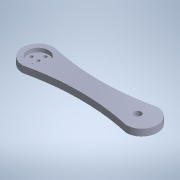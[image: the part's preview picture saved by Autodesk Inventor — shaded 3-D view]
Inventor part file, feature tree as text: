
AUTODESK INVENTOR PART (.ipt)
format: ipt  version: 2020 (Build 240168000, 168)  size: 130,048 bytes
history: mixed  units: mm
features: other x2, extrude x2, sketch x2, imported_body x1
ambient origin geometry x8: Origin, YZ Plane, XZ Plane, XY Plane, X Axis, Y Axis, Z Axis, Center Point
bodies: Body1 (imported_parasolid)
feature tree (7):
  other  "Твердое тело1"
  extrude  "Выдавливание1"  Depth=10.0mm TaperAngle=0.0deg
  extrude  "Выдавливание2"  Depth=7.2mm
  sketch  "Эскиз1"
  sketch  "Эскиз2"
  other  "Cortar-Extruir4"
  imported_body  NMx_Import_Brep_tag  [imported B-rep: ~14 faces, bbox_mm=[114.75, 7.0, 32.5]]
